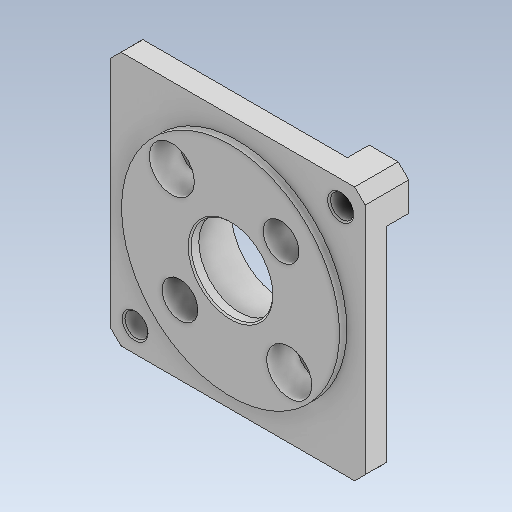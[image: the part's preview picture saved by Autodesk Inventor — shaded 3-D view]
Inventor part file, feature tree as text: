
AUTODESK INVENTOR PART (.ipt)
format: ipt  version: 2023 (Build 270158000, 158)  size: 178,688 bytes
history: native  units: in
note: dims shown in document units (in); Inventor stores cm internally (conversion verified against a paired STEP export)
features: chamfer x1
ambient origin geometry x8: Origin, YZ Plane, XZ Plane, XY Plane, X Axis, Y Axis, Z Axis, Center Point
bodies: Solid1 (feature_tree)
feature tree (1):
  chamfer  "Chamfer1"  [1 undecoded]
note: 1 required parameter value undecoded (feature->parameter linkage not recoverable at this tier; creation-order binding heuristic only, values carry confidence <= 0.55)
